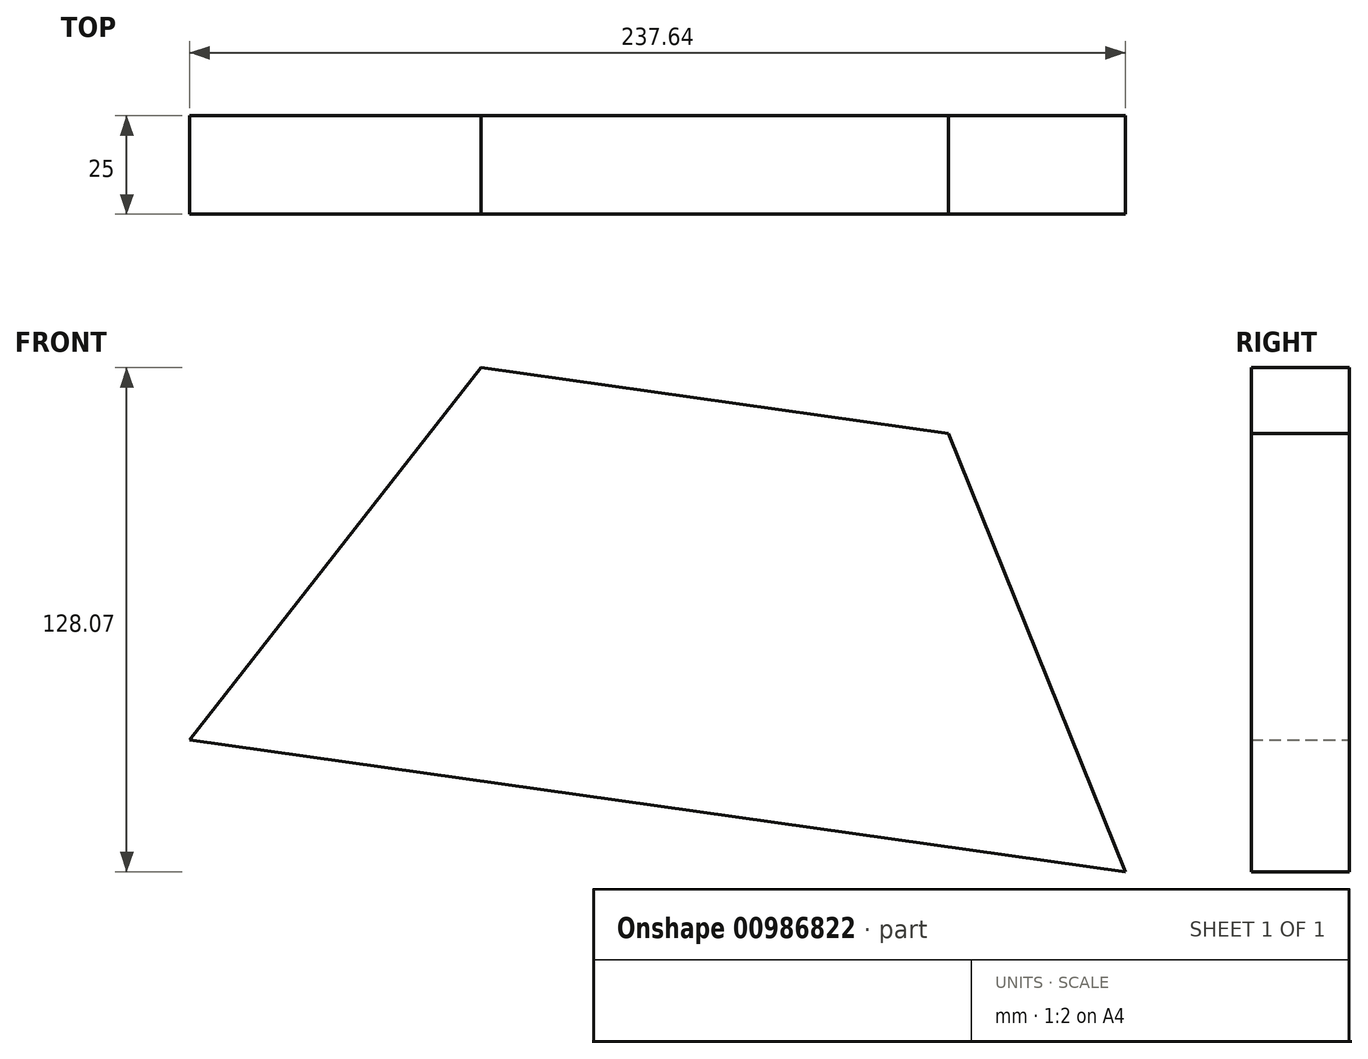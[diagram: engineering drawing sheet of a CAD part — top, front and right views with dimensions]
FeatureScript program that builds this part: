
annotation { "Feature Type Name" : "Feature", "Feature Type Description" : "" }
export const myFeature = defineFeature(function(context is Context, id is Id, definition is map)
    precondition{}
    {
        {
            var Q0;
            Q0=qCreatedBy(makeId("Front.planeOp"),FACE);
            var sketch = newSketch(context, id + "F0", { "sketchPlane" : qUnion([Q0])});
            skLineSegment(sketch, "E0.3", {"start": v(-171.3, 80.82) * mm, "end": v(-97.36, 175.33) * mm});
            skLineSegment(sketch, "E0.4", {"start": v(-97.36, 175.33) * mm, "end": v(21.46, 158.55) * mm});
            skLineSegment(sketch, "E0.5", {"start": v(21.46, 158.55) * mm, "end": v(66.34, 47.26) * mm});
            skPoint(sketch, "E0.0.midPoint", {"position": v(29.37, 0) * mm});
            skLineSegment(sketch, "E1", {"start": v(-171.3, 80.82) * mm, "end": v(66.34, 47.26) * mm});
            skPoint(sketch, "E2.orphan", {"position": v(-7.6, -47.26) * mm});
            skSolve(sketch);
        }
        {
            var Q0;
            Q0 = qSketchRegion(id + "F0", true);
            extrude(context, id + "F1", {"entities" : qUnion([Q0]), "depth" : 25 * mm, "offsetDistance" : 25 * mm});
        }
    });
